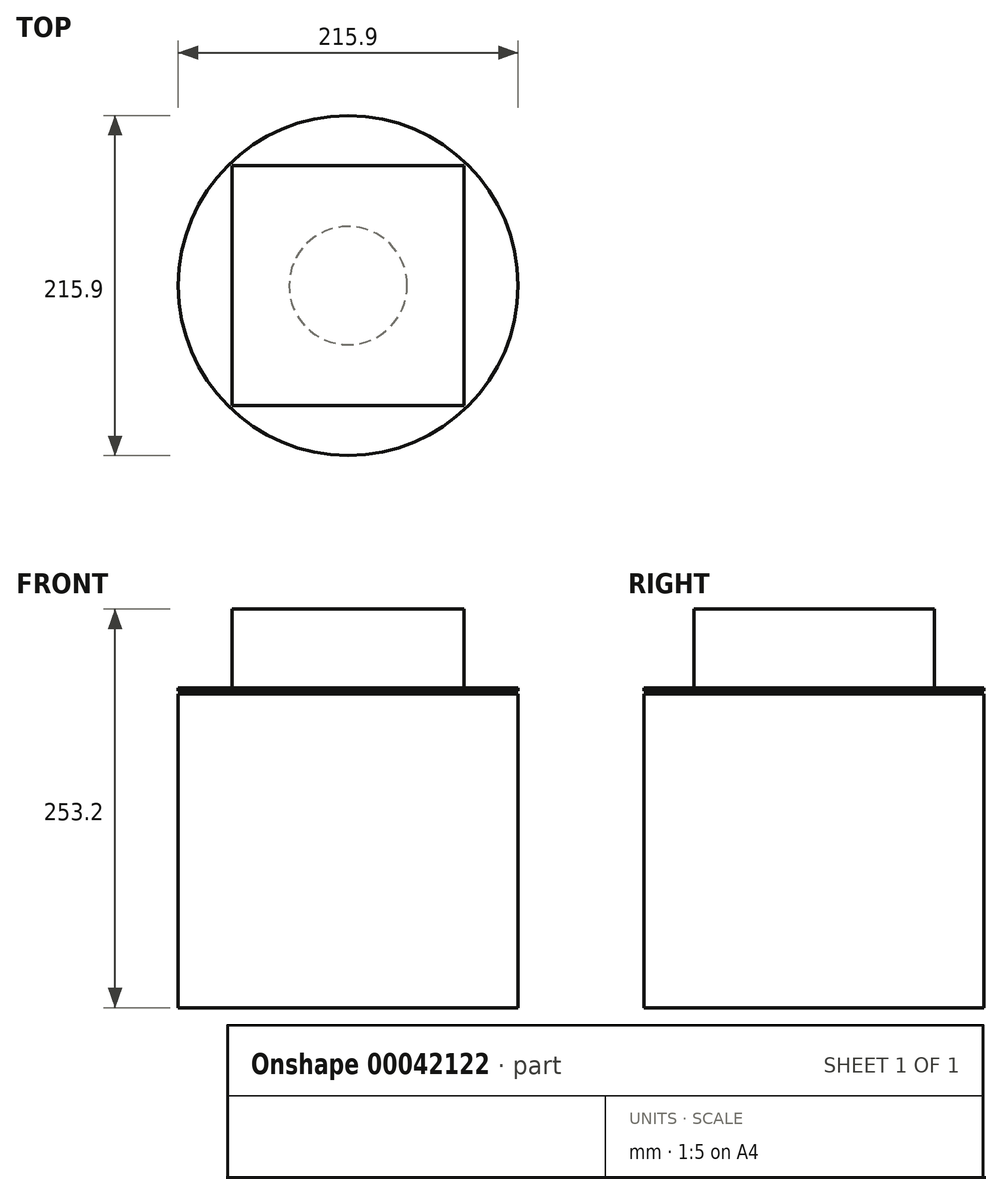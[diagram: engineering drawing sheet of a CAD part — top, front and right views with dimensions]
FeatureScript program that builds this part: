
annotation { "Feature Type Name" : "Feature", "Feature Type Description" : "" }
export const myFeature = defineFeature(function(context is Context, id is Id, definition is map)
    precondition{}
    {
        {
            var Q0;
            Q0=qCreatedBy(makeId("Top.planeOp"),FACE);
            var sketch = newSketch(context, id + "F0", { "sketchPlane" : qUnion([Q0])});
            skCircle(sketch, "E0", {"center": v(-27.1, -39) * mm, "radius": 107.95 * mm});
            skSolve(sketch);
        }
        {
            var Q0;
            Q0 = qSketchRegion(id + "F0", true);
            extrude(context, id + "F1", {"entities" : qUnion([Q0]), "depth" : 199.2 * mm});
        }
        {
            var Q0;
            Q0=makeQuery(id+"F1.opExtrude","CAP_FACE",FACE,{"disambiguationData":[OSD([sQuery(id+"F0.wireOp",EDGE,"E0")])],"isStart":false});
            var sketch = newSketch(context, id + "F2", { "sketchPlane" : qUnion([Q0])});
            skCircle(sketch, "E1", {"center": v(-27.1, -39) * mm, "radius": 37.5 * mm});
            skSolve(sketch);
        }
        {
            var Q0;
            Q0 = qSketchRegion(id + "F2", true);
            extrude(context, id + "F3", {"entities" : qUnion([Q0]), "operationType" : NewBodyOperationType.ADD, "depth" : 2 * mm});
        }
        {
            var Q0;
            Q0=makeQuery(id+"F3.opExtrude","CAP_FACE",FACE,{"disambiguationData":[OSD([sQuery(id+"F2.wireOp",EDGE,"E1")])],"isStart":false});
            var sketch = newSketch(context, id + "F4", { "sketchPlane" : qUnion([Q0])});
            skCircle(sketch, "E2", {"center": v(-27.1, -39) * mm, "radius": 107.95 * mm});
            skSolve(sketch);
        }
        {
            var Q0;
            Q0 = qSketchRegion(id + "F4", true);
            extrude(context, id + "F5", {"entities" : qUnion([Q0]), "operationType" : NewBodyOperationType.ADD, "depth" : 2 * mm});
        }
        {
            var Q0;
            Q0=makeQuery(id+"F5.opExtrude","CAP_FACE",FACE,{"disambiguationData":[OSD([sQuery(id+"F4.wireOp",EDGE,"E2")])],"isStart":false});
            var sketch = newSketch(context, id + "F6", { "sketchPlane" : qUnion([Q0])});
            skLineSegment(sketch, "E3.rect.bottom", {"start": v(46.62, -115.33) * mm, "end": v(-100.8, -115.33) * mm});
            skLineSegment(sketch, "E3.rect.top", {"start": v(46.62, 37.33) * mm, "end": v(-100.8, 37.33) * mm});
            skLineSegment(sketch, "E3.rect.left", {"start": v(46.62, -115.33) * mm, "end": v(46.62, 37.33) * mm});
            skLineSegment(sketch, "E3.rect.right", {"start": v(-100.8, -115.33) * mm, "end": v(-100.8, 37.33) * mm});
            skPoint(sketch, "E3.rect.middle", {"position": v(-27.1, -39) * mm});
            skSolve(sketch);
        }
        {
            var Q0;
            Q0 = qSketchRegion(id + "F6", true);
            extrude(context, id + "F7", {"entities" : qUnion([Q0]), "operationType" : NewBodyOperationType.ADD, "depth" : 50 * mm});
        }
    });
